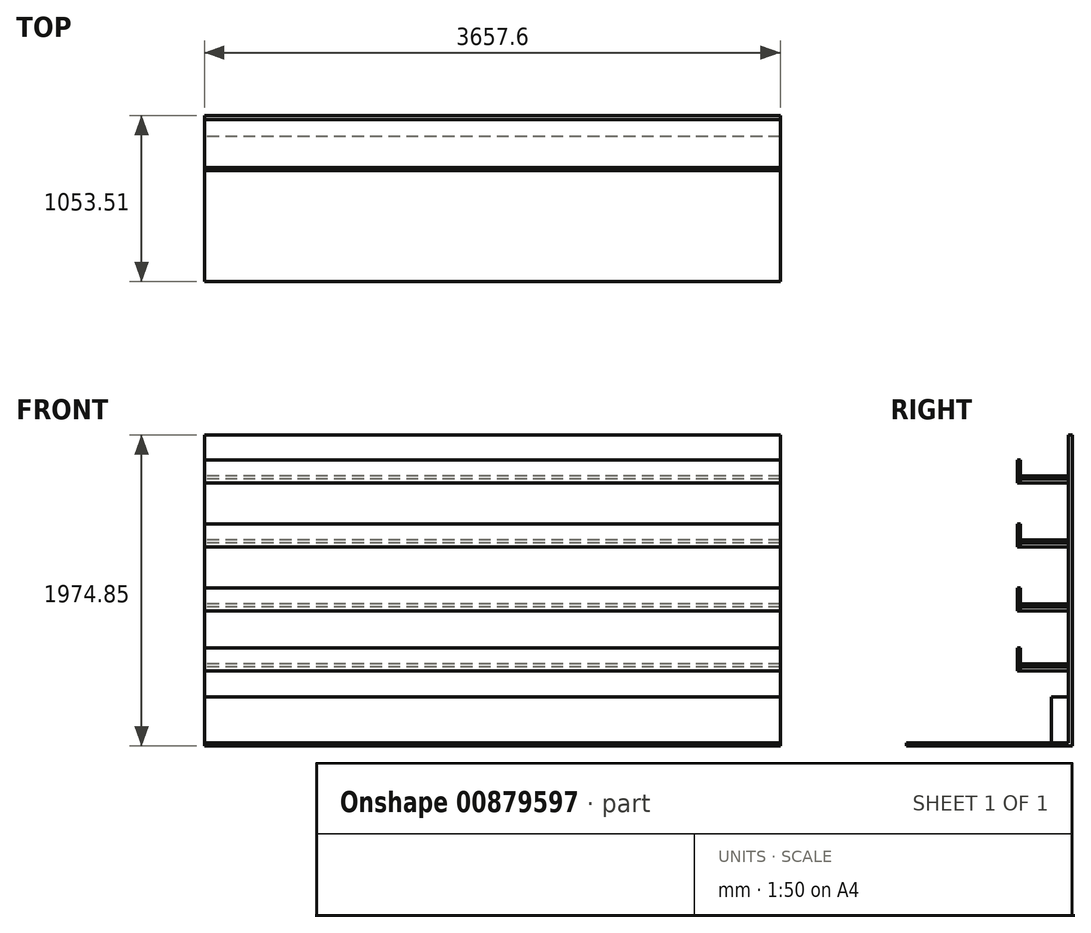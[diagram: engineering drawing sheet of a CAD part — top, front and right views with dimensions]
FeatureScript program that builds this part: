
annotation { "Feature Type Name" : "Feature", "Feature Type Description" : "" }
export const myFeature = defineFeature(function(context is Context, id is Id, definition is map)
    precondition{}
    {
        {
            var Q0;
            Q0=qCreatedBy(makeId("Right.planeOp"),FACE);
            var sketch = newSketch(context, id + "F0", { "sketchPlane" : qUnion([Q0])});
            skLineSegment(sketch, "E0.bottom", {"start": v(0, 0) * mm, "end": v(1828.8, 0) * mm});
            skLineSegment(sketch, "E0.top", {"start": v(0, -19.05) * mm, "end": v(1828.8, -19.05) * mm});
            skLineSegment(sketch, "E0.left", {"start": v(0, 0) * mm, "end": v(0, -19.05) * mm});
            skLineSegment(sketch, "E0.right", {"start": v(1828.8, 0) * mm, "end": v(1828.8, -19.05) * mm});
            skLineSegment(sketch, "E1.bottom", {"start": v(1828.8, 0) * mm, "end": v(1803.4, 0) * mm});
            skLineSegment(sketch, "E1.top", {"start": v(1828.8, 1955.8) * mm, "end": v(1803.4, 1955.8) * mm});
            skLineSegment(sketch, "E1.left", {"start": v(1828.8, 0) * mm, "end": v(1828.8, 1955.8) * mm});
            skLineSegment(sketch, "E1.right", {"start": v(1803.4, 0) * mm, "end": v(1803.4, 1955.8) * mm});
            skSolve(sketch);
        }
        {
            var Q0;
            Q0 = qSketchRegion(id + "F0", true);
            extrude(context, id + "F1", {"entities" : qUnion([Q0]), "depth" : 3657.6 * mm, "offsetDistance" : 25.4 * mm});
        }
        {
            var Q0;
            Q0=makeQuery(id+"F1.opExtrude","CAP_FACE",FACE,{"disambiguationData":[OSD([sQuery(id+"F0.wireOp",EDGE,"E0.bottom"),sQuery(id+"F0.wireOp",EDGE,"E0.top"),sQuery(id+"F0.wireOp",EDGE,"E0.left"),sQuery(id+"F0.wireOp",EDGE,"E0.right"),sQuery(id+"F0.wireOp",EDGE,"E1.top"),sQuery(id+"F0.wireOp",EDGE,"E1.left"),sQuery(id+"F0.wireOp",EDGE,"E1.right")])],"isStart":false});
            var sketch = newSketch(context, id + "F2", { "sketchPlane" : qUnion([Q0])});
            skLineSegment(sketch, "E2.bottom", {"start": v(1803.4, 457.2) * mm, "end": v(1498.6, 457.2) * mm});
            skLineSegment(sketch, "E2.top", {"start": v(1803.4, 482.6) * mm, "end": v(1498.6, 482.6) * mm});
            skLineSegment(sketch, "E2.left", {"start": v(1803.4, 457.2) * mm, "end": v(1803.4, 482.6) * mm});
            skLineSegment(sketch, "E2.right", {"start": v(1498.6, 457.2) * mm, "end": v(1498.6, 482.6) * mm});
            skLineSegment(sketch, "E3.bottom", {"start": v(1803.4, 838.2) * mm, "end": v(1498.6, 838.2) * mm});
            skLineSegment(sketch, "E3.top", {"start": v(1803.4, 863.6) * mm, "end": v(1498.6, 863.6) * mm});
            skLineSegment(sketch, "E3.left", {"start": v(1803.4, 838.2) * mm, "end": v(1803.4, 863.6) * mm});
            skLineSegment(sketch, "E3.right", {"start": v(1498.6, 838.2) * mm, "end": v(1498.6, 863.6) * mm});
            skLineSegment(sketch, "E4.bottom", {"start": v(1803.4, 1244.6) * mm, "end": v(1498.6, 1244.6) * mm});
            skLineSegment(sketch, "E4.top", {"start": v(1803.4, 1270) * mm, "end": v(1498.6, 1270) * mm});
            skLineSegment(sketch, "E4.left", {"start": v(1803.4, 1244.6) * mm, "end": v(1803.4, 1270) * mm});
            skLineSegment(sketch, "E4.right", {"start": v(1498.6, 1244.6) * mm, "end": v(1498.6, 1270) * mm});
            skLineSegment(sketch, "E5.bottom", {"start": v(1803.4, 1651) * mm, "end": v(1498.6, 1651) * mm});
            skLineSegment(sketch, "E5.top", {"start": v(1803.4, 1676.4) * mm, "end": v(1498.6, 1676.4) * mm});
            skLineSegment(sketch, "E5.left", {"start": v(1803.4, 1651) * mm, "end": v(1803.4, 1676.4) * mm});
            skLineSegment(sketch, "E5.right", {"start": v(1498.6, 1651) * mm, "end": v(1498.6, 1676.4) * mm});
            skSolve(sketch);
        }
        {
            var Q0;
            Q0 = qSketchRegion(id + "F2", true);
            extrude(context, id + "F3", {"entities" : qUnion([Q0]), "oppositeDirection" : true, "depth" : 3657.6 * mm, "offsetDistance" : 25.4 * mm});
        }
        {
            var Q0;
            Q0=makeQuery(id+"F3.opExtrude","CAP_FACE",FACE,{"disambiguationData":[OSD([sQuery(id+"F2.wireOp",EDGE,"E3.bottom"),sQuery(id+"F2.wireOp",EDGE,"E3.top"),sQuery(id+"F2.wireOp",EDGE,"E3.left"),sQuery(id+"F2.wireOp",EDGE,"E3.right")])],"isStart":false});
            var sketch = newSketch(context, id + "F4", { "sketchPlane" : qUnion([Q0])});
            skLineSegment(sketch, "E6.bottom", {"start": v(-1498.6, 501.65) * mm, "end": v(-1803.4, 501.65) * mm});
            skLineSegment(sketch, "E6.top", {"start": v(-1498.6, 482.6) * mm, "end": v(-1803.4, 482.6) * mm});
            skLineSegment(sketch, "E6.left", {"start": v(-1498.6, 501.65) * mm, "end": v(-1498.6, 482.6) * mm});
            skLineSegment(sketch, "E6.right", {"start": v(-1803.4, 501.65) * mm, "end": v(-1803.4, 482.6) * mm});
            skLineSegment(sketch, "E7.bottom", {"start": v(-1498.6, 882.65) * mm, "end": v(-1803.4, 882.65) * mm});
            skLineSegment(sketch, "E7.top", {"start": v(-1498.6, 863.6) * mm, "end": v(-1803.4, 863.6) * mm});
            skLineSegment(sketch, "E7.left", {"start": v(-1498.6, 882.65) * mm, "end": v(-1498.6, 863.6) * mm});
            skLineSegment(sketch, "E7.right", {"start": v(-1803.4, 882.65) * mm, "end": v(-1803.4, 863.6) * mm});
            skLineSegment(sketch, "E8.bottom", {"start": v(-1498.6, 1289.05) * mm, "end": v(-1803.4, 1289.05) * mm});
            skLineSegment(sketch, "E8.top", {"start": v(-1498.6, 1270) * mm, "end": v(-1803.4, 1270) * mm});
            skLineSegment(sketch, "E8.left", {"start": v(-1498.6, 1289.05) * mm, "end": v(-1498.6, 1270) * mm});
            skLineSegment(sketch, "E8.right", {"start": v(-1803.4, 1289.05) * mm, "end": v(-1803.4, 1270) * mm});
            skLineSegment(sketch, "E9.bottom", {"start": v(-1498.6, 1695.45) * mm, "end": v(-1803.4, 1695.45) * mm});
            skLineSegment(sketch, "E9.top", {"start": v(-1498.6, 1676.4) * mm, "end": v(-1803.4, 1676.4) * mm});
            skLineSegment(sketch, "E9.left", {"start": v(-1498.6, 1695.45) * mm, "end": v(-1498.6, 1676.4) * mm});
            skLineSegment(sketch, "E9.right", {"start": v(-1803.4, 1695.45) * mm, "end": v(-1803.4, 1676.4) * mm});
            skSolve(sketch);
        }
        {
            var Q0;
            Q0 = qSketchRegion(id + "F4", true);
            extrude(context, id + "F5", {"entities" : qUnion([Q0]), "oppositeDirection" : true, "depth" : 3657.6 * mm, "offsetDistance" : 25.4 * mm});
        }
        {
            var Q0;
            Q0=makeQuery(id+"F3.opExtrude","CAP_FACE",FACE,{"disambiguationData":[OSD([sQuery(id+"F2.wireOp",EDGE,"E5.bottom"),sQuery(id+"F2.wireOp",EDGE,"E5.top"),sQuery(id+"F2.wireOp",EDGE,"E5.left"),sQuery(id+"F2.wireOp",EDGE,"E5.right")])],"isStart":true});
            var sketch = newSketch(context, id + "F6", { "sketchPlane" : qUnion([Q0])});
            skLineSegment(sketch, "E10.bottom", {"start": v(1479.55, 603.25) * mm, "end": v(1498.6, 603.25) * mm});
            skLineSegment(sketch, "E10.top", {"start": v(1479.55, 457.2) * mm, "end": v(1498.6, 457.2) * mm});
            skLineSegment(sketch, "E10.left", {"start": v(1479.55, 603.25) * mm, "end": v(1479.55, 457.2) * mm});
            skLineSegment(sketch, "E10.right", {"start": v(1498.6, 603.25) * mm, "end": v(1498.6, 457.2) * mm});
            skLineSegment(sketch, "E11.bottom", {"start": v(1479.55, 984.25) * mm, "end": v(1498.6, 984.25) * mm});
            skLineSegment(sketch, "E11.top", {"start": v(1479.55, 838.2) * mm, "end": v(1498.6, 838.2) * mm});
            skLineSegment(sketch, "E11.left", {"start": v(1479.55, 984.25) * mm, "end": v(1479.55, 838.2) * mm});
            skLineSegment(sketch, "E11.right", {"start": v(1498.6, 984.25) * mm, "end": v(1498.6, 838.2) * mm});
            skLineSegment(sketch, "E12.bottom", {"start": v(1479.55, 1390.65) * mm, "end": v(1498.6, 1390.65) * mm});
            skLineSegment(sketch, "E12.top", {"start": v(1479.55, 1244.6) * mm, "end": v(1498.6, 1244.6) * mm});
            skLineSegment(sketch, "E12.left", {"start": v(1479.55, 1390.65) * mm, "end": v(1479.55, 1244.6) * mm});
            skLineSegment(sketch, "E12.right", {"start": v(1498.6, 1390.65) * mm, "end": v(1498.6, 1244.6) * mm});
            skLineSegment(sketch, "E13.bottom", {"start": v(1479.55, 1797.05) * mm, "end": v(1498.6, 1797.05) * mm});
            skLineSegment(sketch, "E13.top", {"start": v(1479.55, 1651) * mm, "end": v(1498.6, 1651) * mm});
            skLineSegment(sketch, "E13.left", {"start": v(1479.55, 1797.05) * mm, "end": v(1479.55, 1651) * mm});
            skLineSegment(sketch, "E13.right", {"start": v(1498.6, 1797.05) * mm, "end": v(1498.6, 1651) * mm});
            skSolve(sketch);
        }
        {
            var Q0;
            Q0 = qSketchRegion(id + "F6", true);
            extrude(context, id + "F7", {"entities" : qUnion([Q0]), "oppositeDirection" : true, "depth" : 3657.6 * mm, "offsetDistance" : 25.4 * mm});
        }
        {
            var Q0;
            Q0=makeQuery(id+"F1.opExtrude","CAP_FACE",FACE,{"disambiguationData":[OSD([sQuery(id+"F0.wireOp",EDGE,"E0.bottom"),sQuery(id+"F0.wireOp",EDGE,"E0.top"),sQuery(id+"F0.wireOp",EDGE,"E0.left"),sQuery(id+"F0.wireOp",EDGE,"E0.right"),sQuery(id+"F0.wireOp",EDGE,"E1.top"),sQuery(id+"F0.wireOp",EDGE,"E1.left"),sQuery(id+"F0.wireOp",EDGE,"E1.right")])],"isStart":true});
            var sketch = newSketch(context, id + "F8", { "sketchPlane" : qUnion([Q0])});
            skLineSegment(sketch, "E14.bottom", {"start": v(-1803.4, 292.1) * mm, "end": v(-1695.45, 292.1) * mm});
            skLineSegment(sketch, "E14.top", {"start": v(-1803.4, 0) * mm, "end": v(-1695.45, 0) * mm});
            skLineSegment(sketch, "E14.left", {"start": v(-1803.4, 292.1) * mm, "end": v(-1803.4, 0) * mm});
            skLineSegment(sketch, "E14.right", {"start": v(-1695.45, 292.1) * mm, "end": v(-1695.45, 0) * mm});
            skSolve(sketch);
        }
        {
            var Q0;
            Q0 = qSketchRegion(id + "F8", true);
            extrude(context, id + "F9", {"entities" : qUnion([Q0]), "oppositeDirection" : true, "depth" : 3657.6 * mm, "offsetDistance" : 25.4 * mm});
        }
        {
            var Q0;
            Q0=makeQuery(id+"F1.opExtrude","CAP_FACE",FACE,{"disambiguationData":[OSD([sQuery(id+"F0.wireOp",EDGE,"E0.bottom"),sQuery(id+"F0.wireOp",EDGE,"E0.top"),sQuery(id+"F0.wireOp",EDGE,"E0.left"),sQuery(id+"F0.wireOp",EDGE,"E0.right"),sQuery(id+"F0.wireOp",EDGE,"E1.top"),sQuery(id+"F0.wireOp",EDGE,"E1.left"),sQuery(id+"F0.wireOp",EDGE,"E1.right")])],"isStart":true});
            var sketch = newSketch(context, id + "F10", { "sketchPlane" : qUnion([Q0])});
            skLineSegment(sketch, "E15.bottom", {"start": v(319.26, 1996.97) * mm, "end": v(-775.3, 1996.97) * mm});
            skLineSegment(sketch, "E15.top", {"start": v(319.26, -333.5) * mm, "end": v(-775.3, -333.5) * mm});
            skLineSegment(sketch, "E15.left", {"start": v(319.26, 1996.97) * mm, "end": v(319.26, -333.5) * mm});
            skLineSegment(sketch, "E15.right", {"start": v(-775.3, 1996.97) * mm, "end": v(-775.3, -333.5) * mm});
            skSolve(sketch);
        }
        {
            var Q0;
            Q0 = qSketchRegion(id + "F10", true);
            extrude(context, id + "F11", {"entities" : qUnion([Q0]), "operationType" : NewBodyOperationType.REMOVE, "oppositeDirection" : true, "depth" : 3657.6 * mm, "offsetDistance" : 25.4 * mm});
        }
    });
